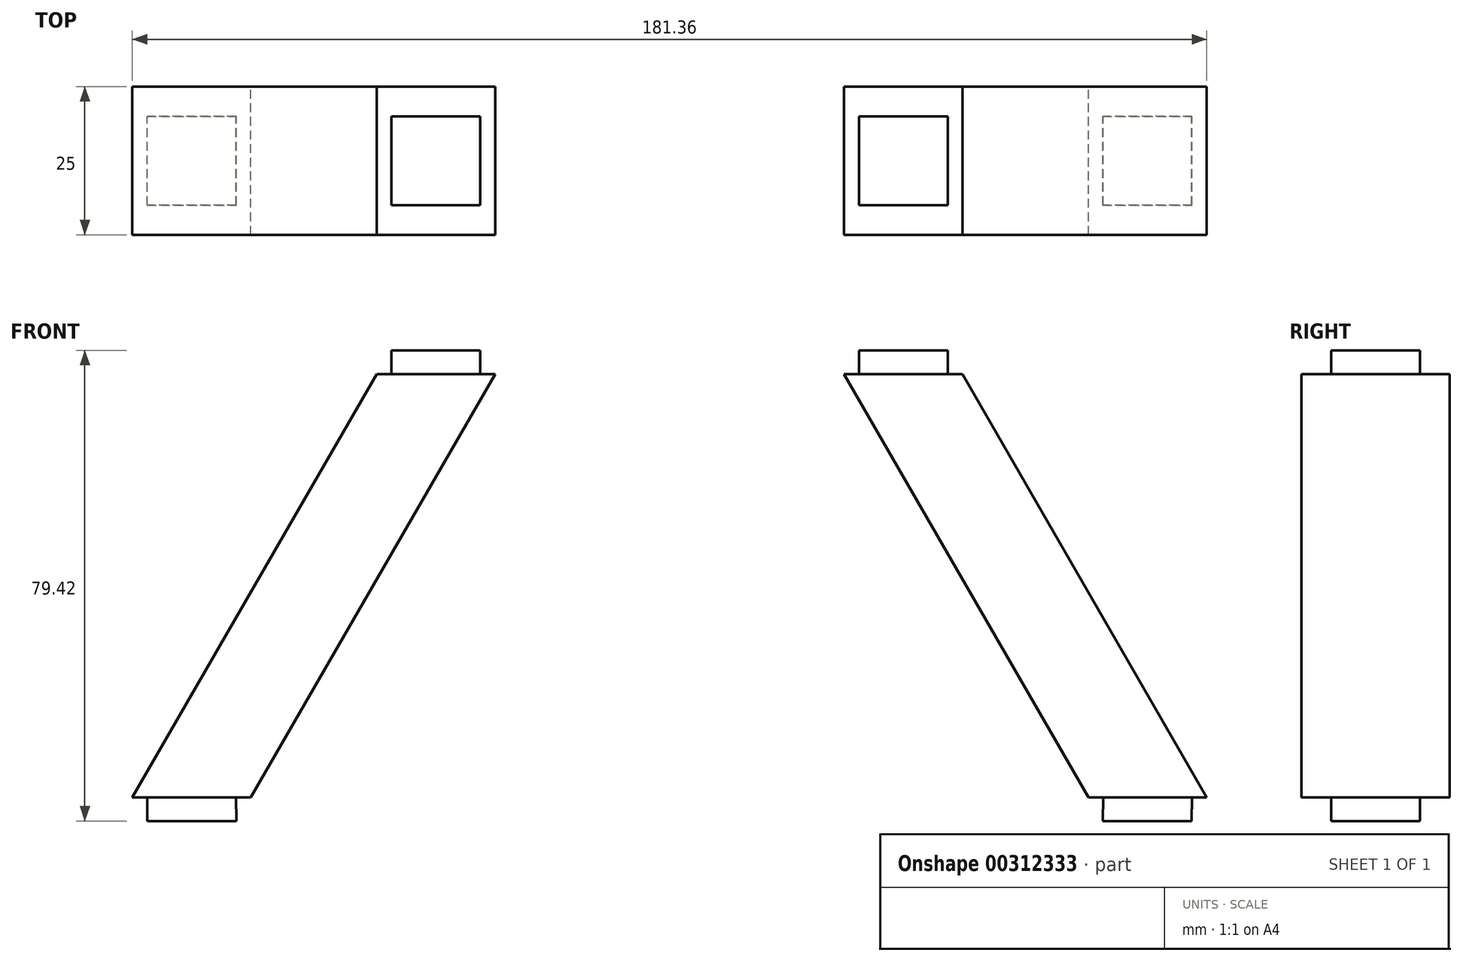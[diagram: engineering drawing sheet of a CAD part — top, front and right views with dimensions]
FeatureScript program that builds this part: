
annotation { "Feature Type Name" : "Feature", "Feature Type Description" : "" }
export const myFeature = defineFeature(function(context is Context, id is Id, definition is map)
    precondition{}
    {
        {
            var Q0;
            Q0=qCreatedBy(makeId("Front.planeOp"),FACE);
            var sketch = newSketch(context, id + "F0", { "sketchPlane" : qUnion([Q0])});
            skLineSegment(sketch, "E0", {"start": v(0, 0) * mm, "end": v(0, 60.48) * mm, "construction": true});
            skLineSegment(sketch, "E1", {"start": v(29.45, 50.43) * mm, "end": v(49.45, 50.43) * mm});
            skLineSegment(sketch, "E2", {"start": v(70.68, -20.99) * mm, "end": v(90.68, -20.99) * mm});
            skLineSegment(sketch, "E3", {"start": v(29.45, 50.43) * mm, "end": v(70.68, -20.99) * mm});
            skLineSegment(sketch, "E4", {"start": v(49.45, 50.43) * mm, "end": v(90.68, -20.99) * mm});
            skLineSegment(sketch, "E5.bottom", {"start": v(46.95, 54.43) * mm, "end": v(31.95, 54.43) * mm});
            skLineSegment(sketch, "E5.left", {"start": v(46.95, 54.43) * mm, "end": v(46.95, 50.43) * mm});
            skLineSegment(sketch, "E5.right", {"start": v(31.95, 54.43) * mm, "end": v(31.95, 50.43) * mm});
            skPoint(sketch, "E5.middle", {"position": v(39.45, 50.43) * mm});
            skLineSegment(sketch, "E6.bottom", {"start": v(88.13, -24.99) * mm, "end": v(73.13, -24.99) * mm});
            skLineSegment(sketch, "E6.left", {"start": v(88.13, -24.99) * mm, "end": v(88.18, -20.99) * mm});
            skLineSegment(sketch, "E6.right", {"start": v(73.13, -24.99) * mm, "end": v(73.18, -20.99) * mm});
            skPoint(sketch, "E6.middle", {"position": v(80.68, -20.99) * mm});
            skPoint(sketch, "E6.top.start.orphan", {"position": v(88.23, -16.99) * mm});
            skPoint(sketch, "E7.orphan", {"position": v(73.23, -16.99) * mm});
            skSolve(sketch);
        }
        {
            var Q0;
            {var subQ7=sQuery(id+"F0.wireOp",EDGE,"E4");Q0=makeQuery(id+"F0.imprint","IMPRINT",FACE,{"disambiguationData":[TD([[makeQuery(id+"F0.imprint","IMPRINT",EDGE,{"derivedFrom":subQ7}),-1.0]])]});}
            extrude(context, id + "F1", {"entities" : qUnion([Q0]), "endBound" : BoundingType.SYMMETRIC, "depth" : 25 * mm});
        }
        {
            var Q0;
            Q0=makeQuery(id+"F0.imprint","IMPRINT",FACE,{"disambiguationData":[TD([[makeQuery(id+"F0.imprint","IMPRINT",EDGE,{"derivedFrom":sQuery(id+"F0.wireOp",EDGE,"E5.bottom")}),1.0]])]});
            var Q1;
            Q1=makeQuery(id+"F0.imprint","IMPRINT",FACE,{"disambiguationData":[TD([[makeQuery(id+"F0.imprint","IMPRINT",EDGE,{"derivedFrom":sQuery(id+"F0.wireOp",EDGE,"E6.bottom")}),-1.0]])]});
            extrude(context, id + "F2", {"entities" : qUnion([Q0, Q1]), "operationType" : NewBodyOperationType.ADD, "endBound" : BoundingType.SYMMETRIC, "depth" : 15 * mm});
        }
        {
            var Q0;
            Q0=makeQuery(id+"F1.opExtrude","SWEPT_BODY",BODY,{"disambiguationData":[OSD([sQuery(id+"F0.wireOp",EDGE,"E1"),sQuery(id+"F0.wireOp",EDGE,"E4"),sQuery(id+"F0.wireOp",EDGE,"E2"),sQuery(id+"F0.wireOp",EDGE,"E3")])]});
            var Q1;
            Q1=qCreatedBy(makeId("Right.planeOp"),FACE);
            mirror(context, id + "F3", {"entities" : qUnion([Q0]), "mirrorPlane" : qUnion([Q1])});
        }
    });
